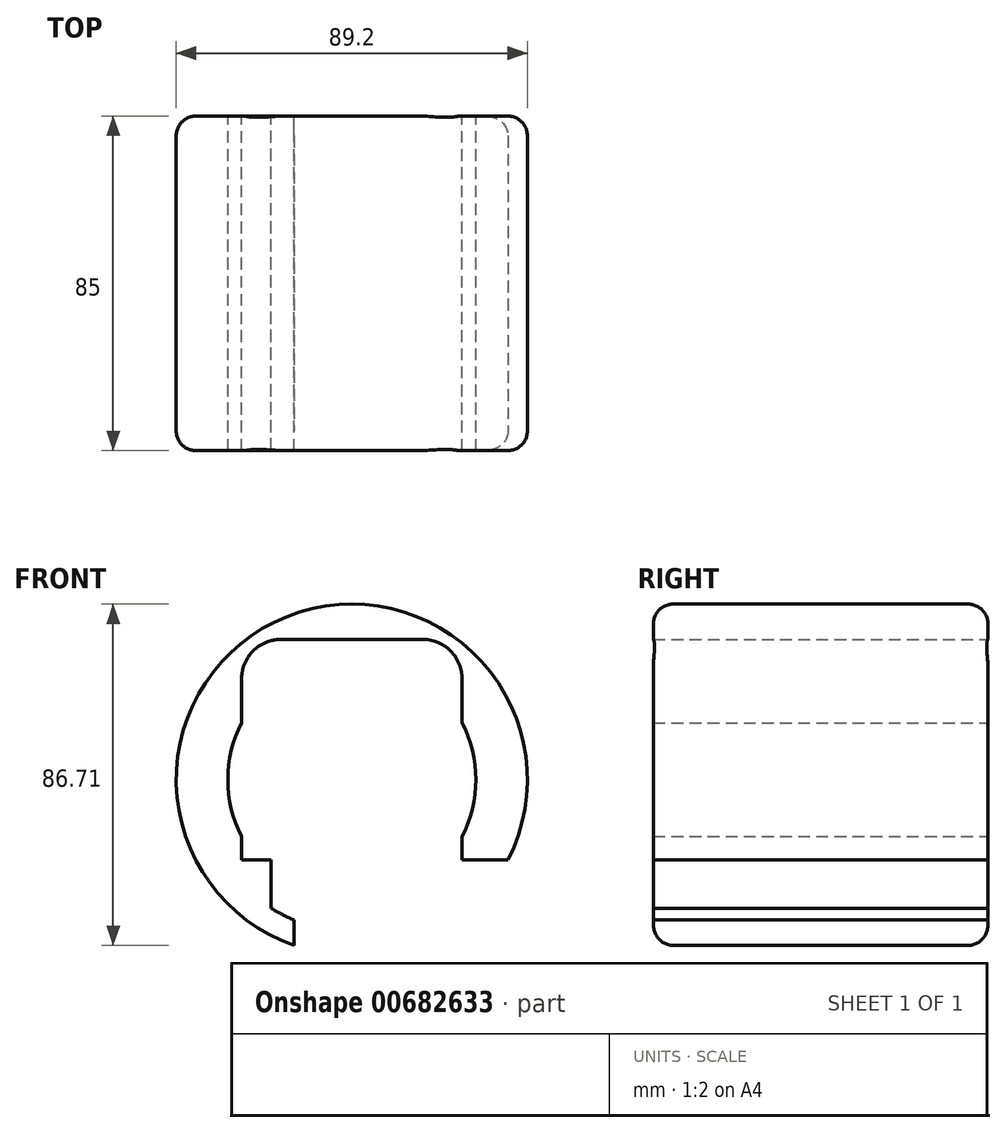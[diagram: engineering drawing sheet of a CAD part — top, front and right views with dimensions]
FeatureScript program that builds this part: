
annotation { "Feature Type Name" : "Feature", "Feature Type Description" : "" }
export const myFeature = defineFeature(function(context is Context, id is Id, definition is map)
    precondition{}
    {
        {
            var Q0;
            Q0=qCreatedBy(makeId("Front.planeOp"),FACE);
            var sketch = newSketch(context, id + "F0", { "sketchPlane" : qUnion([Q0])});
            skLineSegment(sketch, "E0.0.0", {"start": v(48.5, 1.64) * mm, "end": v(48.5, 7.56) * mm});
            skArc(sketch, "E0.0.1", {"start": v(48.5, 7.56) * mm, "mid": v(52, 22) * mm, "end": v(48.5, 36.42) * mm});
            skLineSegment(sketch, "E0.0.2", {"start": v(48.5, 36.42) * mm, "end": v(48.5, 40.64) * mm});
            skLineSegment(sketch, "E0.0.3", {"start": v(48.5, 40.64) * mm, "end": v(-7.5, 40.64) * mm});
            skLineSegment(sketch, "E0.0.4", {"start": v(-7.5, 40.64) * mm, "end": v(-7.5, 1.64) * mm});
            skLineSegment(sketch, "E0.0.5", {"start": v(-7.5, 1.64) * mm, "end": v(0, 1.64) * mm});
            skLineSegment(sketch, "E0.0.6", {"start": v(0, 1.64) * mm, "end": v(0, -10.66) * mm});
            skArc(sketch, "E0.0.7", {"start": v(0, -10.66) * mm, "mid": v(2.85, -12.28) * mm, "end": v(5.83, -13.66) * mm});
            skLineSegment(sketch, "E0.0.8", {"start": v(5.83, -13.66) * mm, "end": v(40.5, -13.66) * mm});
            skArc(sketch, "E0.0.9", {"start": v(40.5, -13.66) * mm, "mid": v(44.04, -12.2) * mm, "end": v(45.5, -8.66) * mm});
            skLineSegment(sketch, "E0.0.10", {"start": v(45.5, -8.66) * mm, "end": v(45.5, 1.64) * mm});
            skLineSegment(sketch, "E0.0.11", {"start": v(45.5, 1.64) * mm, "end": v(48.5, 1.64) * mm});
            skArc(sketch, "E1.0.0", {"start": v(38.5, 57.64) * mm, "mid": v(45.57, 54.71) * mm, "end": v(48.5, 47.64) * mm});
            skLineSegment(sketch, "E1.0.1", {"start": v(38.5, 57.64) * mm, "end": v(2.5, 57.64) * mm});
            skArc(sketch, "E1.0.2", {"start": v(-7.5, 47.64) * mm, "mid": v(-4.57, 54.71) * mm, "end": v(2.5, 57.64) * mm});
            skLineSegment(sketch, "E1.0.3", {"start": v(-7.5, 47.64) * mm, "end": v(-7.5, 45.64) * mm});
            skLineSegment(sketch, "E1.0.4", {"start": v(-7.5, 45.64) * mm, "end": v(48.5, 45.64) * mm});
            skLineSegment(sketch, "E1.0.5", {"start": v(48.5, 45.64) * mm, "end": v(48.5, 47.64) * mm});
            skLineSegment(sketch, "E2.0.0", {"start": v(-7.5, 40.64) * mm, "end": v(-7.5, 45.64) * mm});
            skLineSegment(sketch, "E2.0.2", {"start": v(48.5, 40.64) * mm, "end": v(48.5, 45.64) * mm});
            skLineSegment(sketch, "E2.0.3", {"start": v(48.5, 45.64) * mm, "end": v(-7.5, 45.64) * mm});
            skLineSegment(sketch, "E3.0.0", {"start": v(-7.5, 7.56) * mm, "end": v(-7.5, 36.42) * mm});
            skArc(sketch, "E3.0.1", {"start": v(-7.5, 36.42) * mm, "mid": v(-11, 22) * mm, "end": v(-7.5, 7.56) * mm});
            skCircle(sketch, "E4", {"center": v(20.5, 22) * mm, "radius": 41.6 * mm});
            skCircle(sketch, "E5", {"center": v(20.5, 22) * mm, "radius": 44.6 * mm});
            skSolve(sketch);
        }
        {
            var Q0;
            Q0=makeQuery(id+"F0.imprint","IMPRINT",FACE,{"disambiguationData":[TD([[makeQuery(id+"F0.imprint","IMPRINT",EDGE,{"derivedFrom":sQuery(id+"F0.wireOp",EDGE,"E0.0.0")}),-1.0]])]});
            var Q1;
            Q1=makeQuery(id+"F0.imprint","IMPRINT",FACE,{"disambiguationData":[TD([[makeQuery(id+"F0.imprint","IMPRINT",EDGE,{"derivedFrom":sQuery(id+"F0.wireOp",EDGE,"E4")}),-1.0]])]});
            extrude(context, id + "F1", {"entities" : qUnion([Q0, Q1]), "depth" : 85 * mm, "offsetDistance" : 25 * mm});
        }
        {
            var Q0;
            Q0=makeQuery(id+"F1.opExtrude","CAP_FACE",FACE,{"disambiguationData":[OSD([sQuery(id+"F0.wireOp",EDGE,"E0.0.0"),sQuery(id+"F0.wireOp",EDGE,"E0.0.1"),sQuery(id+"F0.wireOp",EDGE,"E0.0.2"),sQuery(id+"F0.wireOp",EDGE,"E0.0.4"),sQuery(id+"F0.wireOp",EDGE,"E0.0.5"),sQuery(id+"F0.wireOp",EDGE,"E0.0.6"),sQuery(id+"F0.wireOp",EDGE,"E0.0.7"),sQuery(id+"F0.wireOp",EDGE,"E0.0.8"),sQuery(id+"F0.wireOp",EDGE,"E0.0.9"),sQuery(id+"F0.wireOp",EDGE,"E0.0.10"),sQuery(id+"F0.wireOp",EDGE,"E0.0.11"),sQuery(id+"F0.wireOp",EDGE,"E1.0.0"),sQuery(id+"F0.wireOp",EDGE,"E1.0.1"),sQuery(id+"F0.wireOp",EDGE,"E1.0.2"),sQuery(id+"F0.wireOp",EDGE,"E1.0.3"),sQuery(id+"F0.wireOp",EDGE,"E1.0.5"),sQuery(id+"F0.wireOp",EDGE,"E2.0.0"),sQuery(id+"F0.wireOp",EDGE,"E2.0.2"),sQuery(id+"F0.wireOp",EDGE,"E3.0.1"),sQuery(id+"F0.wireOp",EDGE,"E5")])],"isStart":false});
            var sketch = newSketch(context, id + "F2", { "sketchPlane" : qUnion([Q0])});
            skCircle(sketch, "E6.0.0", {"center": v(20.5, 22) * mm, "radius": 44.6 * mm});
            skLineSegment(sketch, "E7", {"start": v(45.5, 1.64) * mm, "end": v(60.18, 1.64) * mm});
            skLineSegment(sketch, "E8", {"start": v(5.83, -13.66) * mm, "end": v(5.83, -20.12) * mm});
            skSolve(sketch);
        }
        {
            var Q0;
            {var subQ0=sQuery(id+"F2.wireOp",EDGE,"E8");Q0=makeQuery(id+"F2.imprint","IMPRINT",FACE,{"disambiguationData":[TD([[makeQuery(id+"F2.imprint","IMPRINT",EDGE,{"derivedFrom":subQ0}),1.0]])]});}
            extrude(context, id + "F3", {"entities" : qUnion([Q0]), "operationType" : NewBodyOperationType.REMOVE, "endBound" : BoundingType.THROUGH_ALL, "oppositeDirection" : true, "depth" : 25 * mm, "offsetDistance" : 25 * mm});
        }
        {
            var Q0;
            Q0=makeQuery(id+"F1.opExtrude","CAP_EDGE",EDGE,{"disambiguationData":[OSD([sQuery(id+"F0.wireOp",EDGE,"E5")])],"isStart":false});
            var Q1;
            Q1=makeQuery(id+"F1.opExtrude","CAP_EDGE",EDGE,{"disambiguationData":[OSD([sQuery(id+"F0.wireOp",EDGE,"E5")])],"isStart":true});
            fillet(context, id + "F4", {"entities" : qUnion([Q0, Q1]), "radius" : 5 * mm, "tangentPropagation" : true, "allowEdgeOverflow" : false});
        }
    });
